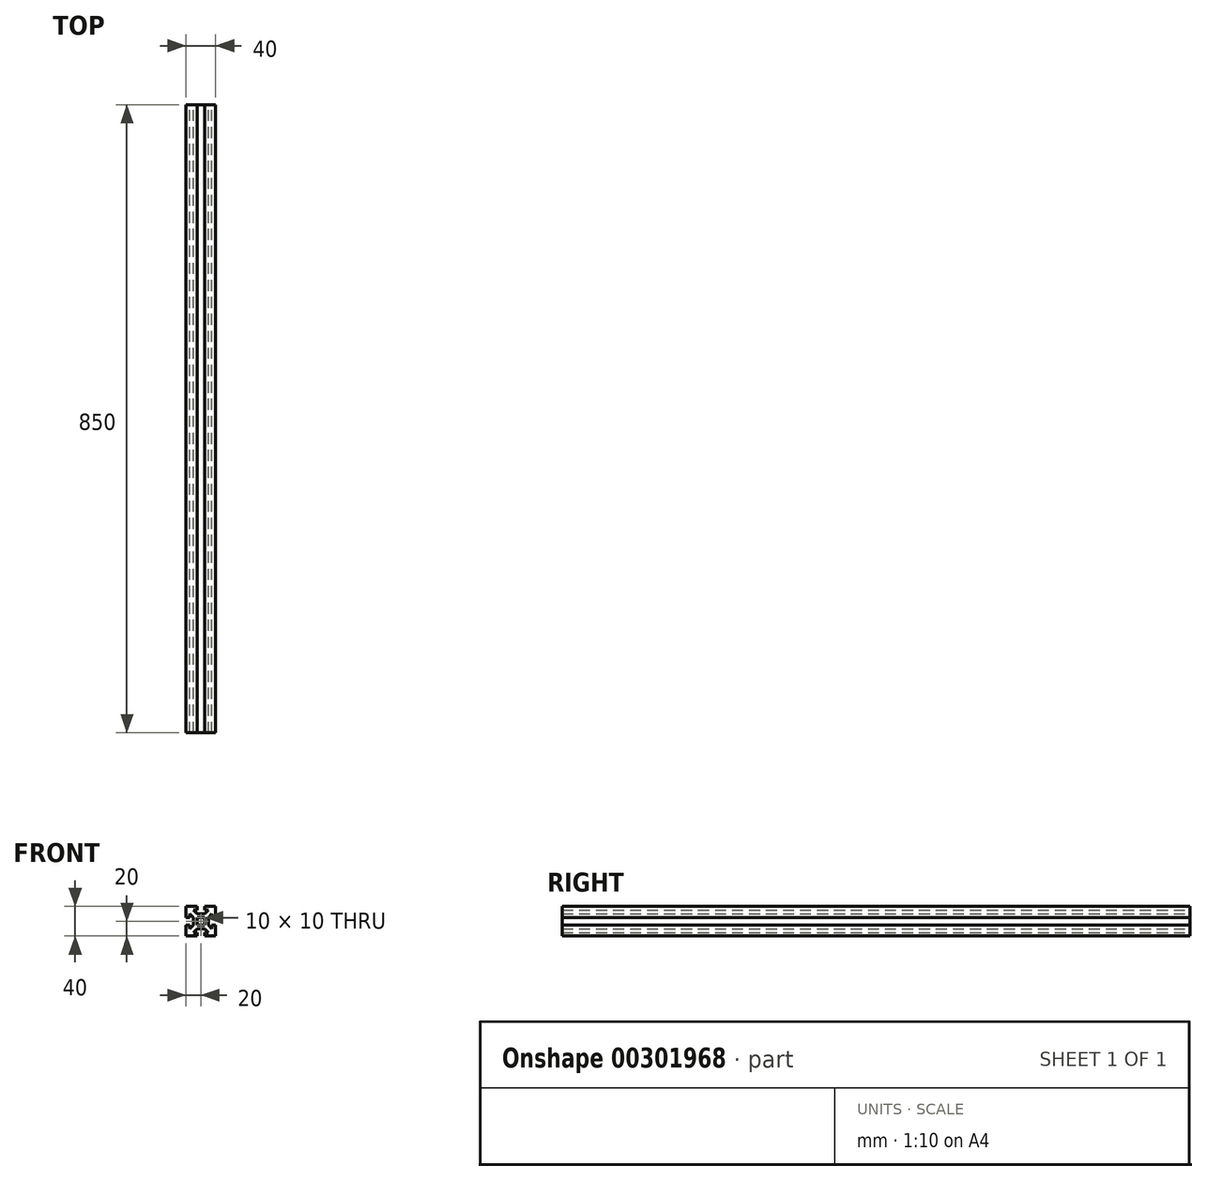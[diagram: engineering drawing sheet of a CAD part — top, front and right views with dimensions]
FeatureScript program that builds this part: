
annotation { "Feature Type Name" : "Feature", "Feature Type Description" : "" }
export const myFeature = defineFeature(function(context is Context, id is Id, definition is map)
    precondition{}
    {
        {
            var Q0;
            Q0=qCreatedBy(makeId("Front.planeOp"),FACE);
            var sketch = newSketch(context, id + "F0", { "sketchPlane" : qUnion([Q0])});
            skLineSegment(sketch, "E0.bottom", {"start": v(20, 20) * mm, "end": v(5, 20) * mm});
            skLineSegment(sketch, "E0.top", {"start": v(20, -20) * mm, "end": v(5, -20) * mm});
            skLineSegment(sketch, "E0.left", {"start": v(20, 20) * mm, "end": v(20, 5) * mm});
            skLineSegment(sketch, "E0.right", {"start": v(-20, 20) * mm, "end": v(-20, 5) * mm});
            skPoint(sketch, "E0.middle", {"position": v(0, 0) * mm});
            skLineSegment(sketch, "E1", {"start": v(0, 20) * mm, "end": v(0, -20) * mm, "construction": true});
            skLineSegment(sketch, "E2", {"start": v(-20, 0) * mm, "end": v(20, 0) * mm, "construction": true});
            skLineSegment(sketch, "E3", {"start": v(-20, 5) * mm, "end": v(-15, 5) * mm});
            skLineSegment(sketch, "E4", {"start": v(-20, -5) * mm, "end": v(-15, -5) * mm});
            skLineSegment(sketch, "E5", {"start": v(-5, 20) * mm, "end": v(-5, 15) * mm});
            skLineSegment(sketch, "E6", {"start": v(5, 20) * mm, "end": v(5, 15) * mm});
            skLineSegment(sketch, "E7", {"start": v(-10, 15) * mm, "end": v(-5, 15) * mm});
            skLineSegment(sketch, "E8", {"start": v(-10, -15) * mm, "end": v(-5, -15) * mm});
            skLineSegment(sketch, "E9", {"start": v(15, 10) * mm, "end": v(15, 5) * mm});
            skLineSegment(sketch, "E10", {"start": v(-15, 10) * mm, "end": v(-10, 5) * mm});
            skLineSegment(sketch, "E11", {"start": v(-10, 15) * mm, "end": v(-5, 10) * mm});
            skLineSegment(sketch, "E12", {"start": v(-15, -10) * mm, "end": v(-10, -5) * mm});
            skLineSegment(sketch, "E13", {"start": v(-10, -15) * mm, "end": v(-5, -10) * mm});
            skLineSegment(sketch, "E14.trimOffspring", {"start": v(20, -5) * mm, "end": v(20, -20) * mm});
            skLineSegment(sketch, "E15.trimOffspring", {"start": v(-20, -5) * mm, "end": v(-20, -20) * mm});
            skLineSegment(sketch, "E16.trimOffspring", {"start": v(-5, -20) * mm, "end": v(-20, -20) * mm});
            skLineSegment(sketch, "E17.trimOffspring", {"start": v(-5, 20) * mm, "end": v(-20, 20) * mm});
            skLineSegment(sketch, "E18.trimOffspring", {"start": v(5, 15) * mm, "end": v(10, 15) * mm});
            skLineSegment(sketch, "E19.trimOffspring", {"start": v(-15, -5) * mm, "end": v(-15, -10) * mm});
            skLineSegment(sketch, "E20.trimOffspring", {"start": v(15, -5) * mm, "end": v(15, -10) * mm});
            skLineSegment(sketch, "E21.trimOffspring", {"start": v(5, -15) * mm, "end": v(10, -15) * mm});
            skLineSegment(sketch, "E22.trimOffspring", {"start": v(-5, 5) * mm, "end": v(-5, -5) * mm});
            skLineSegment(sketch, "E23.trimOffspring", {"start": v(5, 5) * mm, "end": v(5, -5) * mm});
            skLineSegment(sketch, "E24.trimOffspring", {"start": v(15, 5) * mm, "end": v(20, 5) * mm});
            skLineSegment(sketch, "E25.trimOffspring", {"start": v(15, -5) * mm, "end": v(20, -5) * mm});
            skLineSegment(sketch, "E26.trimOffspring", {"start": v(5, -15) * mm, "end": v(5, -20) * mm});
            skLineSegment(sketch, "E27.trimOffspring", {"start": v(-5, -15) * mm, "end": v(-5, -20) * mm});
            skLineSegment(sketch, "E28.trimOffspring", {"start": v(-5, -5) * mm, "end": v(5, -5) * mm});
            skLineSegment(sketch, "E29.trimOffspring", {"start": v(-5, 5) * mm, "end": v(5, 5) * mm});
            skLineSegment(sketch, "E30", {"start": v(10, 5) * mm, "end": v(10, -5) * mm});
            skLineSegment(sketch, "E31", {"start": v(-5, 10) * mm, "end": v(5, 10) * mm});
            skLineSegment(sketch, "E32", {"start": v(-10, 5) * mm, "end": v(-10, -5) * mm});
            skLineSegment(sketch, "E33", {"start": v(-5, -10) * mm, "end": v(5, -10) * mm});
            skLineSegment(sketch, "E34.trimOffspring", {"start": v(-15, 10) * mm, "end": v(-15, 5) * mm});
            skPoint(sketch, "E35.orphan", {"position": v(20, 15) * mm});
            skPoint(sketch, "E36.orphan", {"position": v(20, -15) * mm});
            skPoint(sketch, "E37.orphan", {"position": v(15, -20) * mm});
            skPoint(sketch, "E38.orphan", {"position": v(-15, -20) * mm});
            skLineSegment(sketch, "E39.trimOffspring", {"start": v(-5, 0) * mm, "end": v(0, -5) * mm});
            skLineSegment(sketch, "E40.trimOffspring", {"start": v(-5, 0) * mm, "end": v(0, 5) * mm});
            skLineSegment(sketch, "E41.trimOffspring", {"start": v(0, 5) * mm, "end": v(5, 0) * mm});
            skLineSegment(sketch, "E42.trimOffspring", {"start": v(5, 10) * mm, "end": v(10, 15) * mm});
            skLineSegment(sketch, "E43.trimOffspring", {"start": v(10, 5) * mm, "end": v(15, 10) * mm});
            skLineSegment(sketch, "E44.trimOffspring", {"start": v(10, -5) * mm, "end": v(15, -10) * mm});
            skLineSegment(sketch, "E45.trimOffspring", {"start": v(5, -10) * mm, "end": v(10, -15) * mm});
            skLineSegment(sketch, "E46.trimOffspring", {"start": v(0, -5) * mm, "end": v(5, 0) * mm});
            skSolve(sketch);
        }
        {
            var Q0;
            Q0=makeQuery(id+"F0.imprint","IMPRINT",FACE,{"disambiguationData":[TD([[makeQuery(id+"F0.imprint","IMPRINT",EDGE,{"derivedFrom":sQuery(id+"F0.wireOp",EDGE,"E0.bottom")}),1.0]])]});
            extrude(context, id + "F1", {"entities" : qUnion([Q0]), "depth" : 850 * mm});
        }
    });
